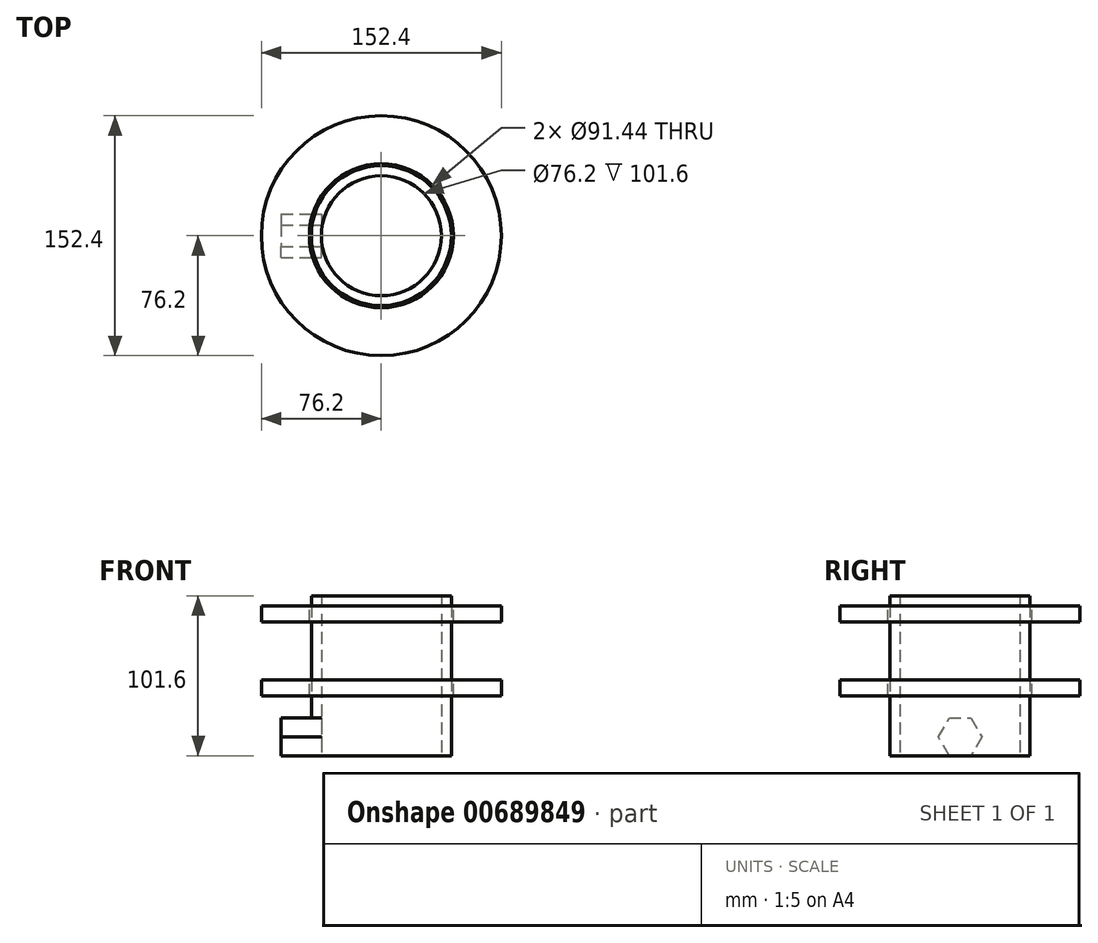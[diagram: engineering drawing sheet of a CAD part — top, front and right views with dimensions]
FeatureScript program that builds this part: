
annotation { "Feature Type Name" : "Feature", "Feature Type Description" : "" }
export const myFeature = defineFeature(function(context is Context, id is Id, definition is map)
    precondition{}
    {
        {
            var Q0;
            Q0=qCreatedBy(makeId("Top.planeOp"),FACE);
            var sketch = newSketch(context, id + "F0", { "sketchPlane" : qUnion([Q0])});
            skCircle(sketch, "E0", {"center": v(0, 0) * mm, "radius": 38.1 * mm});
            skCircle(sketch, "E1", {"center": v(0, 0) * mm, "radius": 44.45 * mm});
            skSolve(sketch);
        }
        {
            var Q0;
            Q0 = qSketchRegion(id + "F0", true);
            extrude(context, id + "F1", {"entities" : qUnion([Q0]), "endBound" : BoundingType.SYMMETRIC, "depth" : 101.6 * mm, "offsetDistance" : 25.4 * mm});
        }
        {
            var Q0;
            Q0=makeQuery(id+"F1.opExtrude","CAP_FACE",FACE,{"disambiguationData":[OSD([sQuery(id+"F0.wireOp",EDGE,"E0"),sQuery(id+"F0.wireOp",EDGE,"E1")])],"isStart":false});
            cPlane(context, id + "F2", {"entities" : qUnion([Q0]), "cplaneType" : CPlaneType.OFFSET, "offset" : 6.35 * mm, "oppositeDirection" : true, "width" : 152.4 * mm, "height" : 152.4 * mm});
        }
        {
            var Q0;
            Q0=qCreatedBy(id+"F2.planeOp",FACE);
            var sketch = newSketch(context, id + "F3", { "sketchPlane" : qUnion([Q0])});
            skCircle(sketch, "E2", {"center": v(0, 0) * mm, "radius": 76.2 * mm});
            skCircle(sketch, "E3", {"center": v(0, 0) * mm, "radius": 45.72 * mm});
            skSolve(sketch);
        }
        {
            var Q0;
            Q0 = qSketchRegion(id + "F3", true);
            extrude(context, id + "F4", {"entities" : qUnion([Q0]), "oppositeDirection" : true, "depth" : 10.16 * mm, "offsetDistance" : 25.4 * mm});
        }
        {
            var Q0;
            Q0=makeQuery(id+"F4.opExtrude","CAP_FACE",FACE,{"disambiguationData":[OSD([sQuery(id+"F3.wireOp",EDGE,"E2"),sQuery(id+"F3.wireOp",EDGE,"E3")])],"isStart":false});
            cPlane(context, id + "F5", {"entities" : qUnion([Q0]), "cplaneType" : CPlaneType.OFFSET, "offset" : 36.83 * mm, "width" : 152.4 * mm, "height" : 152.4 * mm});
        }
        {
            var Q0;
            Q0=qCreatedBy(id+"F5.planeOp",FACE);
            var sketch = newSketch(context, id + "F6", { "sketchPlane" : qUnion([Q0])});
            skCircle(sketch, "E4.0", {"center": v(0, 0) * mm, "radius": 45.72 * mm});
            skCircle(sketch, "E5.0", {"center": v(0, 0) * mm, "radius": 76.2 * mm});
            skSolve(sketch);
        }
        {
            var Q0;
            Q0 = qSketchRegion(id + "F6", true);
            extrude(context, id + "F7", {"entities" : qUnion([Q0]), "depth" : 10.16 * mm, "offsetDistance" : 25.4 * mm});
        }
        {
            var Q0;
            Q0=qCreatedBy(makeId("Right.planeOp"),FACE);
            var sketch = newSketch(context, id + "F8", { "sketchPlane" : qUnion([Q0])});
            skCircle(sketch, "E6.cCircle", {"center": v(0, -38.86) * mm, "radius": 11.94 * mm, "construction": true});
            skLineSegment(sketch, "E6.0", {"start": v(6.9, -50.8) * mm, "end": v(-6.9, -50.8) * mm});
            skLineSegment(sketch, "E6.1", {"start": v(-6.9, -50.8) * mm, "end": v(-13.78, -38.86) * mm});
            skLineSegment(sketch, "E6.2", {"start": v(-13.78, -38.86) * mm, "end": v(-6.9, -26.92) * mm});
            skLineSegment(sketch, "E6.3", {"start": v(-6.9, -26.92) * mm, "end": v(6.9, -26.92) * mm});
            skLineSegment(sketch, "E6.4", {"start": v(6.9, -26.92) * mm, "end": v(13.78, -38.86) * mm});
            skLineSegment(sketch, "E6.5", {"start": v(13.78, -38.86) * mm, "end": v(6.9, -50.8) * mm});
            skPoint(sketch, "E6.0.midPoint", {"position": v(0, -50.8) * mm});
            skSolve(sketch);
        }
        {
            var Q0;
            Q0 = qSketchRegion(id + "F8", true);
            extrude(context, id + "F9", {"entities" : qUnion([Q0]), "oppositeDirection" : true, "depth" : 63.5 * mm, "offsetDistance" : 25.4 * mm, "hasSecondDirection" : true, "secondDirectionOppositeDirection" : true, "secondDirectionDepth" : 38.1 * mm});
        }
    });
